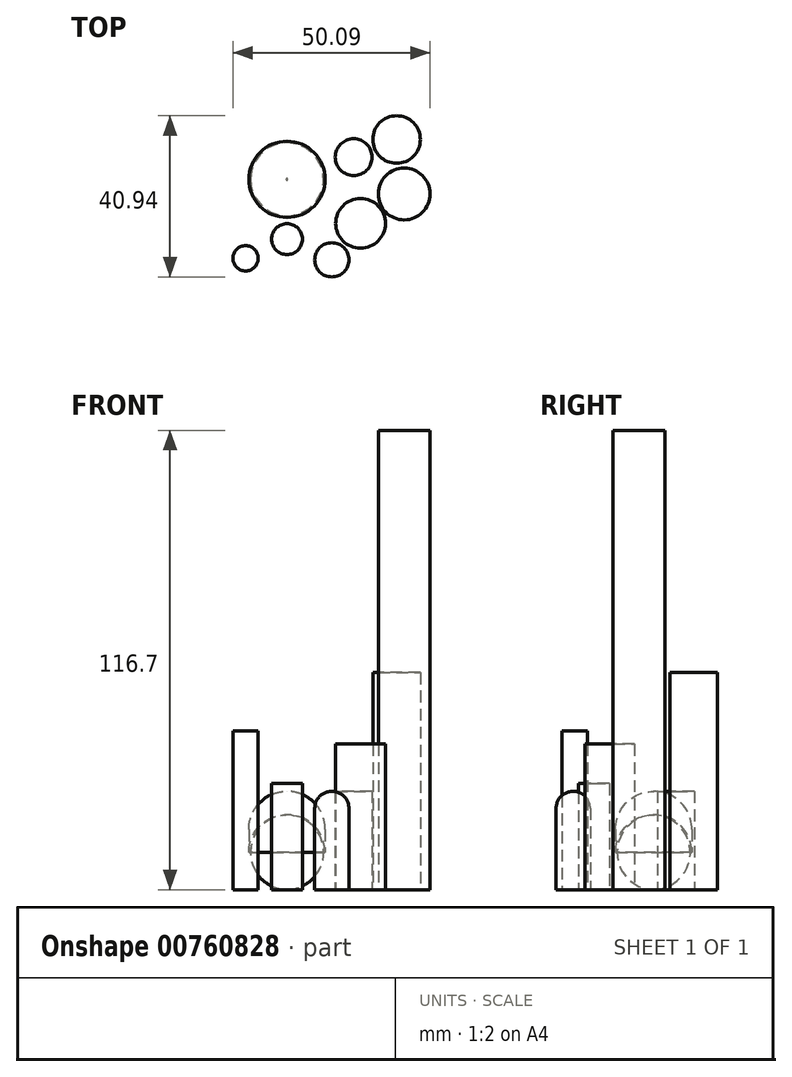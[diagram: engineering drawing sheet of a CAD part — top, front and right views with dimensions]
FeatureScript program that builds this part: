
annotation { "Feature Type Name" : "Feature", "Feature Type Description" : "" }
export const myFeature = defineFeature(function(context is Context, id is Id, definition is map)
    precondition{}
    {
        {
            var Q0;
            Q0=qCreatedBy(makeId("Top.planeOp"),FACE);
            var sketch = newSketch(context, id + "F0", { "sketchPlane" : qUnion([Q0])});
            skCircle(sketch, "E0", {"center": v(-11.39, 11.2) * mm, "radius": 9.7 * mm});
            skCircle(sketch, "E1", {"center": v(5.55, 16.84) * mm, "radius": 4.68 * mm});
            skCircle(sketch, "E2", {"center": v(7.3, 0) * mm, "radius": 6.31 * mm});
            skCircle(sketch, "E3", {"center": v(-21.9, -8.86) * mm, "radius": 3.21 * mm});
            skCircle(sketch, "E4", {"center": v(-11.39, -4) * mm, "radius": 3.91 * mm});
            skCircle(sketch, "E5", {"center": v(0, -9.25) * mm, "radius": 4.34 * mm});
            skCircle(sketch, "E6", {"center": v(16.45, 21.32) * mm, "radius": 6.04 * mm});
            skCircle(sketch, "E7", {"center": v(18.4, 7.5) * mm, "radius": 6.59 * mm});
            skSolve(sketch);
        }
        {
            var Q0;
            Q0 = qSketchRegion(id + "F0", true);
            extrude(context, id + "F1", {"entities" : qUnion([Q0]), "depth" : 25 * mm, "offsetDistance" : 25 * mm});
        }
        {
            var Q0;
            Q0=makeQuery(id+"F1.opExtrude","CAP_EDGE",EDGE,{"disambiguationData":[OSD([sQuery(id+"F0.wireOp",EDGE,"E5")])],"isStart":false});
            fillet(context, id + "F2", {"entities" : qUnion([Q0]), "radius" : 4.3 * mm, "tangentPropagation" : true, "allowEdgeOverflow" : false});
        }
        {
            var Q0;
            Q0=makeQuery(id+"F1.opExtrude","CAP_EDGE",EDGE,{"disambiguationData":[OSD([sQuery(id+"F0.wireOp",EDGE,"E0")])],"isStart":false});
            fillet(context, id + "F3", {"entities" : qUnion([Q0]), "radius" : 9.66 * mm, "tangentPropagation" : true, "allowEdgeOverflow" : false});
        }
        {
            var Q0;
            Q0=makeQuery(id+"F1.opExtrude","CAP_FACE",FACE,{"disambiguationData":[OSD([sQuery(id+"F0.wireOp",EDGE,"E0")])],"isStart":true});
            fillet(context, id + "F4", {"entities" : qUnion([Q0]), "radius" : 9.5 * mm, "tangentPropagation" : true, "allowEdgeOverflow" : false});
        }
        {
            var Q0;
            Q0=makeQuery(id+"F1.opExtrude","CAP_FACE",FACE,{"disambiguationData":[OSD([sQuery(id+"F0.wireOp",EDGE,"E6")])],"isStart":false});
            extrude(context, id + "F5", {"entities" : qUnion([Q0]), "operationType" : NewBodyOperationType.ADD, "depth" : 30.2 * mm, "offsetDistance" : 25 * mm});
        }
        {
            var Q0;
            Q0=makeQuery(id+"F1.opExtrude","CAP_FACE",FACE,{"disambiguationData":[OSD([sQuery(id+"F0.wireOp",EDGE,"E3")])],"isStart":false});
            extrude(context, id + "F6", {"entities" : qUnion([Q0]), "operationType" : NewBodyOperationType.ADD, "oppositeDirection" : true, "depth" : 12.6 * mm, "offsetDistance" : 25 * mm});
        }
        {
            var Q0;
            Q0=makeQuery(id+"F1.opExtrude","CAP_FACE",FACE,{"disambiguationData":[OSD([sQuery(id+"F0.wireOp",EDGE,"E3")])],"isStart":false});
            extrude(context, id + "F7", {"entities" : qUnion([Q0]), "operationType" : NewBodyOperationType.ADD, "depth" : 15.4 * mm, "offsetDistance" : 25 * mm});
        }
        {
            var Q0;
            Q0=makeQuery(id+"F1.opExtrude","CAP_FACE",FACE,{"disambiguationData":[OSD([sQuery(id+"F0.wireOp",EDGE,"E4")])],"isStart":false});
            extrude(context, id + "F8", {"entities" : qUnion([Q0]), "operationType" : NewBodyOperationType.ADD, "depth" : 2 * mm, "offsetDistance" : 25 * mm});
        }
        {
            var Q0;
            Q0=makeQuery(id+"F1.opExtrude","CAP_FACE",FACE,{"disambiguationData":[OSD([sQuery(id+"F0.wireOp",EDGE,"E7")])],"isStart":false});
            extrude(context, id + "F9", {"entities" : qUnion([Q0]), "operationType" : NewBodyOperationType.ADD, "depth" : 91.7 * mm, "offsetDistance" : 25 * mm});
        }
        {
            var Q0;
            Q0=makeQuery(id+"F1.opExtrude","CAP_FACE",FACE,{"disambiguationData":[OSD([sQuery(id+"F0.wireOp",EDGE,"E2")])],"isStart":false});
            extrude(context, id + "F10", {"entities" : qUnion([Q0]), "operationType" : NewBodyOperationType.ADD, "depth" : 12 * mm, "offsetDistance" : 25 * mm});
        }
    });
